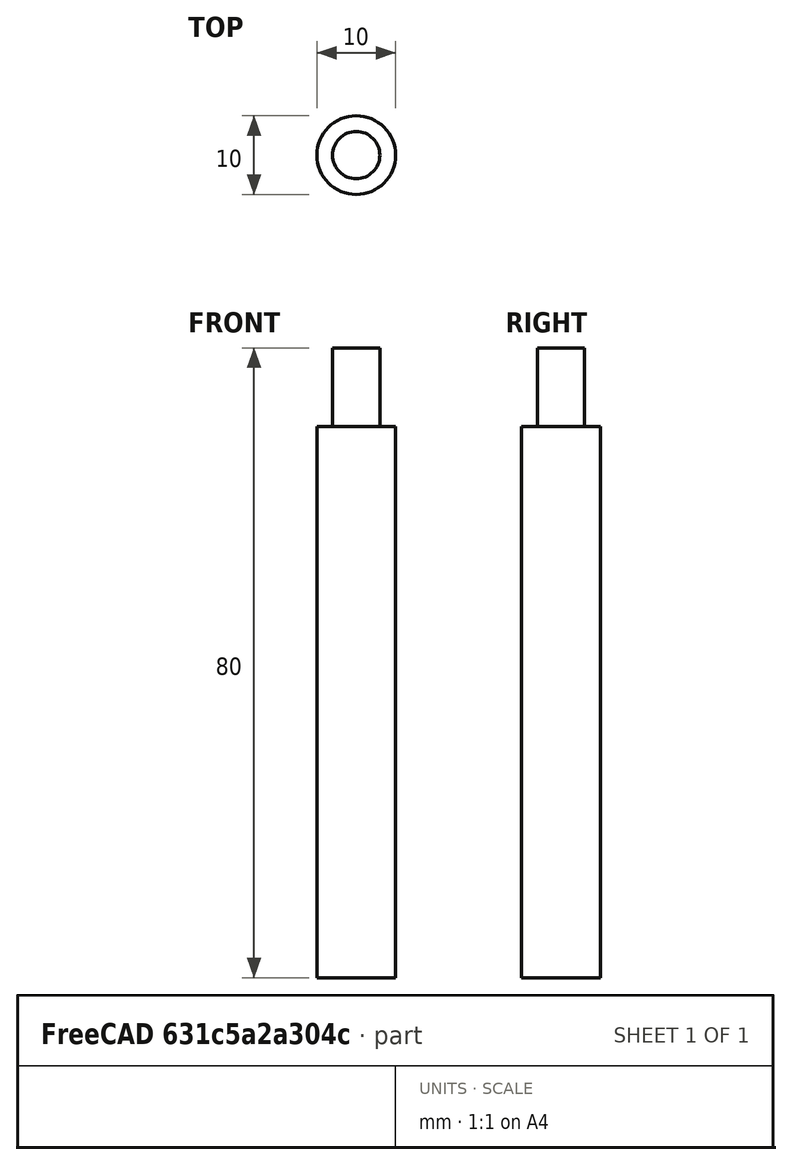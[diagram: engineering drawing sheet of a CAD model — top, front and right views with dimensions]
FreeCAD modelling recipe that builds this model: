
FCSTD DOCUMENT  (FreeCAD 0.14R3702 (Git))
Label: shaft
License: CC-BY 3.0
LicenseURL: http://creativecommons.org/licenses/by/3.0/
objects: Part::Cylinder×2, Sketcher::SketchObject×1
note: 3 computed .brp shape members not serialized (recipe doc carries the construction recipe); baked Part::Feature solids carry a one-line shape summary decoded from their .brp

FEATURE [Sketcher::SketchObject] Sketch
  sketch-geometry (4):
    g0: ArcOfCircle CenterX=-47.3019 CenterY=0.183981 CenterZ=0 NormalX=0 NormalY=0 NormalZ=1 Radius=1.45314 StartAngle=1.5708 EndAngle=4.71239
    g1: ArcOfCircle CenterX=55.9468 CenterY=0.183981 CenterZ=0 NormalX=0 NormalY=0 NormalZ=1 Radius=1.45314 StartAngle=4.71239 EndAngle=7.85398
    g2: LineSegment StartX=-47.3019 StartY=-1.26916 StartZ=0 EndX=55.9468 EndY=-1.26916 EndZ=0
    g3: LineSegment StartX=-47.3019 StartY=1.63712 StartZ=0 EndX=55.9468 EndY=1.63712 EndZ=0
  constraints (10):
    c: Tangent(g0,g2)
    c: Tangent(g0,g3)
    c: Tangent(g1,g2)
    c: Tangent(g1,g3)
    c: Coincident(g0,g3)
    c: Coincident(g0,g2)
    c: Coincident(g2,g1)
    c: Coincident(g3,g1)
    c: Horizontal(g2)
    c: Equal(g0,g1)
FEATURE [Part::Cylinder] Cylinder
  Angle = 360
  Height = 70
  Radius = 5
FEATURE [Part::Cylinder] Cylinder001
  Angle = 360
  Height = 10
  Placement = pos=(0,0,70) rot=(0,0,1;0rad)
  Radius = 3
